# Revit family: 63_UN_LEDPanel_RTP-XM 1196x296_Norton
name_source: partatom
category: Lighting Fixtures
units: mm (PartAtom-declared; Revit-internal decimal feet)

## family parameters
Always vertical = Yes
Cut with Voids When Loaded = No
Light Source = Yes
OmniClass Number = 23.80.70.11.14.11
OmniClass Title = Downlights
Part Type = Normal
Room Calculation Point = Yes
Round Connector Dimension = Use Diameter
Shared = No
Work Plane-Based = No

## types (4) — shared parameters
Assembly Code = 63.0
Calc_L1_Symbol = 12 mm  [stored 0.0393701 ft]
Calc_L2_Symbol = 3 mm  [stored 0.00984252 ft]
Color Filter = 16777215
Dimming Lamp Color Temperature Shift = <None>
ETIM Code = -
Emit Shape Visible in Rendering = No
Emit from Rectangle Length = 244 mm  [stored 0.800525 ft]
Emit from Rectangle Width = 1170 mm  [stored 3.83858 ft]
GTIN Code = -
H1 = 51 mm
Housing_Material = Laminate, White
IK Value = IK07
IP Value = IP20
ISBN Code = -
IfcExportAs = IfcLightFixtureType
IfcExportType = USERDEFINED
L1 = 1196 mm  [stored 3.92388 ft]
L2 = 270 mm
L3 = 13 mm
Lamp = LED
Manufacturer = Norton
Model = RTP-XM
Tilt Angle = 90.00°
Type Comments = 1196x296
URL = https://www.ivlibrary.com
Voltage = 230 V

## per-type parameters (varying)
| type | Apparent Load | Luminous Flux (lm) | Photometric Web File | Wattage Comments |
| RTP-XM LED 83 2 4450LM GST | 37 VA | 4450 lm | RTPXMLED832NLM4450_LDT.ies | 37W |
| RTP-XM LED 83 2 4450LM GST NOOD | 45 VA | 4500 lm | RTPXMLED832NLM4450_LDT.ies | 45W |
| RTP-XM LED 84 2 4650LM GST | 37 VA | 4650 lm | RTPXMLED842NLM4650_LDT.ies | 37W |
| RTP-XM LED 84 2 4650LM GST NOOD | 37 VA | 4650 lm | RTPXMLED842NLM4650_LDT.ies | 37W |

note: [stored X ft] marks values corroborated as IEEE doubles in the binary element streams (Revit-internal decimal feet)

## geometry (parser evidence)
native form markers: Sweep x4
no freeform markers — native parametric forms only
